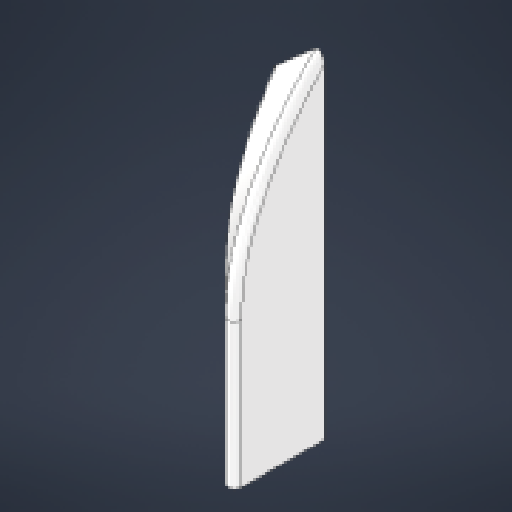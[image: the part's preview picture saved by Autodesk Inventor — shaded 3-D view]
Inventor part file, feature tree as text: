
AUTODESK INVENTOR PART (.ipt)
format: ipt  version: 2024.3 (Build 283343010, 343A)  size: 183,808 bytes
history: native  units: in
note: dims shown in document units (in); Inventor stores cm internally (conversion verified against a paired STEP export)
features: sketch x3, extrude x2, fillet x2, chamfer x1, hole x1
ambient origin geometry x8: Origin, YZ Plane, XZ Plane, XY Plane, X Axis, Y Axis, Z Axis, Center Point
bodies: Solid1 (feature_tree)
feature tree (9):
  extrude  "Extrusion1"  Depth=3.3in
  extrude  "Extrusion2"  Depth=0.5in
  chamfer  "Chamfer1"  [1 undecoded]
  fillet  "Fillet1"  Radius=3.0in
  fillet  "Fillet3"  Radius=0.0625in
  hole  "Hole3"  [1 undecoded]
  sketch  "Sketch1"  dims[d3=1.0in d4=3.3in]
  sketch  "Sketch2"  dims[d5=0.5in d6=0.0in d7=4.5in d8=0.0in d9=0.0in]
  sketch  "Sketch6"  dims[d10=0.6762in d11=0.5in d12=45.0deg d13=3.0in d33=0.0625in d50=1.1811in d52=0.75in d53=0.3937in d55=1.0in d57=0.25in d58=0.5in d59=0.2114in d60=0.75in d61=0.375in d62=0.25in d63=0.5635in d64=0.2362in d65=0.8108in]
note: 2 required parameter values undecoded (feature->parameter linkage not recoverable at this tier; creation-order binding heuristic only, values carry confidence <= 0.55)
